# Revit family: 1434003 Pinhole Round Adjustable Fire-Rated
name_source: partatom
category: Lighting Fixtures
units: mm (PartAtom-declared; Revit-internal decimal feet)

## family parameters
Always vertical = Yes
Cut with Voids When Loaded = No
Host = Ceiling
Light Source = No
OmniClass Number = 23.80.70.11
OmniClass Title = Luminaries for Internal Lighting
Part Type = Normal
Room Calculation Point = No
Round Connector Dimension = Use Diameter
Shared = No

## types (1)
- CE
    ADA compliant = Not Applicable
    Default Elevation = 0 mm  [stored 0 ft]
    Dimmable = Lamp Dependent
    Dimming Method = Lamp Dependent
    Driver Included = Not Applicable
    Driver Required = No
    Efficacy (lm/w) = Lamp Dependent
    Electrical Class = II
    Lamp = GU10 LED
    Length of supplied cable = See Datasheet
    Light Source Fixed = Replaceable
    Location / IP Rating = IP20
    Main Finish = Matt White
    Main Material = Metal - Mild Steel
    Manufacturer URL - Europe and Rest of World = www.astrolighting.com
    Manufacturer URL - North America = us.astrolighting.com
    Max Drop (pendants) = Not Applicable
    Power (Watts) = 6W MAX
    Product CCT = Lamp Dependent
    Product CRI = Lamp Dependent
    Product Dimensions (MM) = See Datasheet
    Product Location = Indoor
    Product Name = Pinhole Round Adjustable Fire Rated
    Product SKU = 1434003
    Product Weight (KG) = 0 mm  [stored 0 ft]

note: [stored X ft] marks values corroborated as IEEE doubles in the binary element streams (Revit-internal decimal feet)

## geometry (parser evidence)
native form markers: Sweep x3
no freeform markers — native parametric forms only
